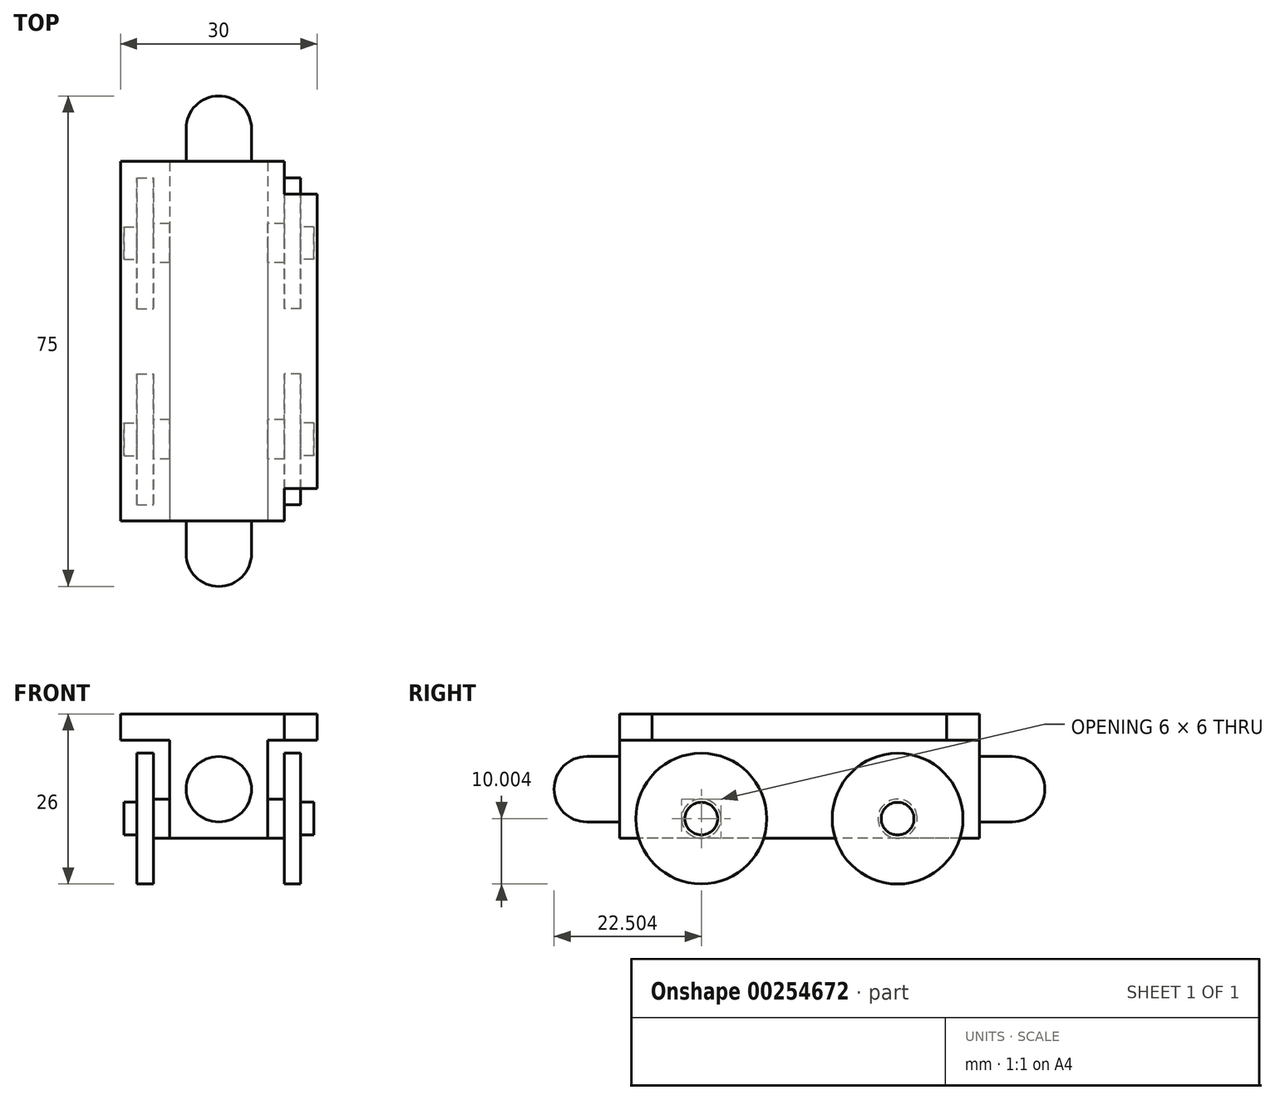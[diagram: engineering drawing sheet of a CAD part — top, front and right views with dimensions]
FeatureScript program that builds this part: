
annotation { "Feature Type Name" : "Feature", "Feature Type Description" : "" }
export const myFeature = defineFeature(function(context is Context, id is Id, definition is map)
    precondition{}
    {
        {
            var Q0;
            Q0=qCreatedBy(makeId("Top.planeOp"),FACE);
            var sketch = newSketch(context, id + "F0", { "sketchPlane" : qUnion([Q0])});
            skLineSegment(sketch, "E0.bottom", {"start": v(7.5, 27.5) * mm, "end": v(-7.5, 27.5) * mm});
            skLineSegment(sketch, "E0.top", {"start": v(7.5, -27.5) * mm, "end": v(-7.5, -27.5) * mm});
            skLineSegment(sketch, "E0.left", {"start": v(7.5, 27.5) * mm, "end": v(7.5, -27.5) * mm});
            skLineSegment(sketch, "E0.right", {"start": v(-7.5, 27.5) * mm, "end": v(-7.5, -27.5) * mm});
            skPoint(sketch, "E0.middle", {"position": v(0, 0) * mm});
            skSolve(sketch);
        }
        {
            var Q0;
            Q0 = qSketchRegion(id + "F0", true);
            extrude(context, id + "F1", {"entities" : qUnion([Q0]), "oppositeDirection" : true, "depth" : 15 * mm});
        }
        {
            var Q0;
            Q0=qCreatedBy(makeId("Top.planeOp"),FACE);
            var sketch = newSketch(context, id + "F2", { "sketchPlane" : qUnion([Q0])});
            skLineSegment(sketch, "E1.bottom", {"start": v(15, 27.5) * mm, "end": v(-15, 27.5) * mm});
            skLineSegment(sketch, "E1.top", {"start": v(15, -27.5) * mm, "end": v(-15, -27.5) * mm});
            skLineSegment(sketch, "E1.left", {"start": v(15, 27.5) * mm, "end": v(15, -27.5) * mm});
            skLineSegment(sketch, "E1.right", {"start": v(-15, 27.5) * mm, "end": v(-15, -27.5) * mm});
            skPoint(sketch, "E1.middle", {"position": v(0, 0) * mm});
            skSolve(sketch);
        }
        {
            var Q0;
            Q0 = qSketchRegion(id + "F2", true);
            extrude(context, id + "F3", {"entities" : qUnion([Q0]), "operationType" : NewBodyOperationType.ADD, "depth" : 4 * mm});
        }
        {
            var Q0;
            Q0=qCreatedBy(makeId("Top.planeOp"),FACE);
            var sketch = newSketch(context, id + "F4", { "sketchPlane" : qUnion([Q0])});
            skPoint(sketch, "E2.0", {"position": v(15, -27.5) * mm});
            skPoint(sketch, "E3.0", {"position": v(15, 27.5) * mm});
            skLineSegment(sketch, "E4", {"start": v(15, -27.5) * mm, "end": v(10, -27.5) * mm});
            skLineSegment(sketch, "E5", {"start": v(15, -27.5) * mm, "end": v(15, -22.5) * mm});
            skLineSegment(sketch, "E6.bottom", {"start": v(15, -22.5) * mm, "end": v(10, -22.5) * mm});
            skLineSegment(sketch, "E6.left", {"start": v(15, -22.5) * mm, "end": v(15, -27.5) * mm});
            skLineSegment(sketch, "E6.right", {"start": v(10, -22.5) * mm, "end": v(10, -27.5) * mm});
            skSolve(sketch);
        }
        {
            var Q0;
            Q0 = qSketchRegion(id + "F4", true);
            extrude(context, id + "F5", {"entities" : qUnion([Q0]), "operationType" : NewBodyOperationType.REMOVE, "depth" : 25 * mm});
        }
        {
            var Q0;
            Q0=qCreatedBy(makeId("Top.planeOp"),FACE);
            var sketch = newSketch(context, id + "F6", { "sketchPlane" : qUnion([Q0])});
            skPoint(sketch, "E7.0", {"position": v(15, 27.5) * mm});
            skLineSegment(sketch, "E8", {"start": v(15, 27.5) * mm, "end": v(10, 27.5) * mm});
            skLineSegment(sketch, "E9", {"start": v(15, 27.5) * mm, "end": v(15, 22.5) * mm});
            skLineSegment(sketch, "E10.bottom", {"start": v(10, 27.5) * mm, "end": v(15, 27.5) * mm});
            skLineSegment(sketch, "E10.top", {"start": v(10, 22.5) * mm, "end": v(15, 22.5) * mm});
            skLineSegment(sketch, "E10.left", {"start": v(10, 27.5) * mm, "end": v(10, 22.5) * mm});
            skSolve(sketch);
        }
        {
            var Q0;
            Q0 = qSketchRegion(id + "F6", true);
            extrude(context, id + "F7", {"entities" : qUnion([Q0]), "operationType" : NewBodyOperationType.REMOVE, "depth" : 25 * mm});
        }
        {
            var Q0;
            Q0=makeQuery(id+"F3.boolean.opBoolean","MERGE",FACE,{"derivedFrom":[makeQuery(id+"F1.opExtrude","SWEPT_FACE",FACE,{"disambiguationData":[OSD([sQuery(id+"F0.wireOp",EDGE,"E0.top")])]}),makeQuery(id+"F3.opExtrude","SWEPT_FACE",FACE,{"disambiguationData":[OSD([sQuery(id+"F2.wireOp",EDGE,"E1.top")])]})]});
            var sketch = newSketch(context, id + "F8", { "sketchPlane" : qUnion([Q0])});
            skLineSegment(sketch, "E11", {"start": v(0, -15) * mm, "end": v(0, -7.5) * mm, "construction": true});
            skPoint(sketch, "E11.endSnap0", {"position": v(0, -15) * mm});
            skCircle(sketch, "E12", {"center": v(0, -7.5) * mm, "radius": 5 * mm});
            skSolve(sketch);
        }
        {
            var Q0;
            Q0 = qSketchRegion(id + "F8", true);
            extrude(context, id + "F9", {"entities" : qUnion([Q0]), "operationType" : NewBodyOperationType.ADD, "depth" : 5 * mm});
        }
        {
            var Q0;
            Q0=makeQuery(id+"F3.boolean.opBoolean","MERGE",FACE,{"derivedFrom":[makeQuery(id+"F1.opExtrude","SWEPT_FACE",FACE,{"disambiguationData":[OSD([sQuery(id+"F0.wireOp",EDGE,"E0.bottom")])]}),makeQuery(id+"F3.opExtrude","SWEPT_FACE",FACE,{"disambiguationData":[OSD([sQuery(id+"F2.wireOp",EDGE,"E1.bottom")])]})]});
            var sketch = newSketch(context, id + "F10", { "sketchPlane" : qUnion([Q0])});
            skLineSegment(sketch, "E13", {"start": v(0, -15) * mm, "end": v(0, -7.5) * mm, "construction": true});
            skPoint(sketch, "E13.endSnap0", {"position": v(0, -15) * mm});
            skCircle(sketch, "E14", {"center": v(0, -7.5) * mm, "radius": 5 * mm});
            skSolve(sketch);
        }
        {
            var Q0;
            Q0 = qSketchRegion(id + "F10", true);
            extrude(context, id + "F11", {"entities" : qUnion([Q0]), "operationType" : NewBodyOperationType.ADD, "depth" : 5 * mm});
        }
        {
            var Q0;
            Q0=qCreatedBy(makeId("Right.planeOp"),FACE);
            var sketch = newSketch(context, id + "F12", { "sketchPlane" : qUnion([Q0])});
            skLineSegment(sketch, "E15", {"start": v(-27.5, -15) * mm, "end": v(-15, -15) * mm, "construction": true});
            skLineSegment(sketch, "E16", {"start": v(-15, -15) * mm, "end": v(-15, -12) * mm, "construction": true});
            skCircle(sketch, "E17", {"center": v(-15, -12) * mm, "radius": 3 * mm});
            skSolve(sketch);
        }
        {
            var Q0;
            Q0 = qSketchRegion(id + "F12", true);
            extrude(context, id + "F13", {"entities" : qUnion([Q0]), "operationType" : NewBodyOperationType.ADD, "endBound" : BoundingType.SYMMETRIC, "depth" : 20 * mm});
        }
        {
            var Q0;
            Q0=qCreatedBy(makeId("Right.planeOp"),FACE);
            var sketch = newSketch(context, id + "F14", { "sketchPlane" : qUnion([Q0])});
            skPoint(sketch, "E18.0", {"position": v(27.5, -15) * mm});
            skLineSegment(sketch, "E19", {"start": v(27.5, -15) * mm, "end": v(15, -15) * mm, "construction": true});
            skLineSegment(sketch, "E20", {"start": v(15, -15) * mm, "end": v(15, -12) * mm, "construction": true});
            skCircle(sketch, "E21", {"center": v(15, -12) * mm, "radius": 3 * mm});
            skSolve(sketch);
        }
        {
            var Q0;
            Q0 = qSketchRegion(id + "F14", true);
            extrude(context, id + "F15", {"entities" : qUnion([Q0]), "operationType" : NewBodyOperationType.ADD, "endBound" : BoundingType.SYMMETRIC, "depth" : 20 * mm});
        }
        {
            var Q0;
            Q0=makeQuery(id+"F13.opExtrude","CAP_FACE",FACE,{"disambiguationData":[OSD([sQuery(id+"F12.wireOp",EDGE,"E17")])],"isStart":false});
            var sketch = newSketch(context, id + "F16", { "sketchPlane" : qUnion([Q0])});
            skPoint(sketch, "E22", {"position": v(-15, -12) * mm});
            skCircle(sketch, "E23", {"center": v(-15, -12) * mm, "radius": 10 * mm});
            skSolve(sketch);
        }
        {
            var Q0;
            Q0 = qSketchRegion(id + "F16", true);
            extrude(context, id + "F17", {"entities" : qUnion([Q0]), "operationType" : NewBodyOperationType.ADD, "depth" : 2.5 * mm});
        }
        {
            var Q0;
            Q0=makeQuery(id+"F15.opExtrude","CAP_FACE",FACE,{"disambiguationData":[OSD([sQuery(id+"F14.wireOp",EDGE,"E21")])],"isStart":false});
            var sketch = newSketch(context, id + "F18", { "sketchPlane" : qUnion([Q0])});
            skPoint(sketch, "E24", {"position": v(15, -12) * mm});
            skCircle(sketch, "E25", {"center": v(15, -12) * mm, "radius": 10 * mm});
            skSolve(sketch);
        }
        {
            var Q0;
            Q0 = qSketchRegion(id + "F18", true);
            extrude(context, id + "F19", {"entities" : qUnion([Q0]), "operationType" : NewBodyOperationType.ADD, "depth" : 2.5 * mm});
        }
        {
            var Q0;
            Q0=makeQuery(id+"F15.opExtrude","CAP_FACE",FACE,{"disambiguationData":[OSD([sQuery(id+"F14.wireOp",EDGE,"E21")])],"isStart":true});
            var sketch = newSketch(context, id + "F20", { "sketchPlane" : qUnion([Q0])});
            skPoint(sketch, "E26", {"position": v(-15, -12) * mm});
            skCircle(sketch, "E27", {"center": v(-15, -12) * mm, "radius": 10 * mm});
            skSolve(sketch);
        }
        {
            var Q0;
            Q0 = qSketchRegion(id + "F20", true);
            extrude(context, id + "F21", {"entities" : qUnion([Q0]), "operationType" : NewBodyOperationType.ADD, "depth" : 2.5 * mm});
        }
        {
            var Q0;
            Q0=makeQuery(id+"F13.opExtrude","CAP_FACE",FACE,{"disambiguationData":[OSD([sQuery(id+"F12.wireOp",EDGE,"E17")])],"isStart":true});
            var sketch = newSketch(context, id + "F22", { "sketchPlane" : qUnion([Q0])});
            skPoint(sketch, "E28", {"position": v(15, -12) * mm});
            skCircle(sketch, "E29", {"center": v(15, -12) * mm, "radius": 10 * mm});
            skSolve(sketch);
        }
        {
            var Q0;
            Q0 = qSketchRegion(id + "F22", true);
            extrude(context, id + "F23", {"entities" : qUnion([Q0]), "operationType" : NewBodyOperationType.ADD, "depth" : 2.5 * mm});
        }
        {
            var Q0;
            Q0=makeQuery(id+"F17.opExtrude","CAP_FACE",FACE,{"disambiguationData":[OSD([sQuery(id+"F16.wireOp",EDGE,"E23")])],"isStart":false});
            var sketch = newSketch(context, id + "F24", { "sketchPlane" : qUnion([Q0])});
            skPoint(sketch, "E30", {"position": v(-15, -12) * mm});
            skCircle(sketch, "E31", {"center": v(-15, -12) * mm, "radius": 2.5 * mm});
            skSolve(sketch);
        }
        {
            var Q0;
            Q0 = qSketchRegion(id + "F24", true);
            extrude(context, id + "F25", {"entities" : qUnion([Q0]), "operationType" : NewBodyOperationType.ADD, "depth" : 2 * mm});
        }
        {
            var Q0;
            Q0=makeQuery(id+"F19.opExtrude","CAP_FACE",FACE,{"disambiguationData":[OSD([sQuery(id+"F18.wireOp",EDGE,"E25")])],"isStart":false});
            var sketch = newSketch(context, id + "F26", { "sketchPlane" : qUnion([Q0])});
            skPoint(sketch, "E32", {"position": v(15, -12) * mm});
            skCircle(sketch, "E33", {"center": v(15, -12) * mm, "radius": 2.5 * mm});
            skSolve(sketch);
        }
        {
            var Q0;
            Q0 = qSketchRegion(id + "F26", true);
            extrude(context, id + "F27", {"entities" : qUnion([Q0]), "operationType" : NewBodyOperationType.ADD, "depth" : 2 * mm});
        }
        {
            var Q0;
            Q0=makeQuery(id+"F23.opExtrude","CAP_FACE",FACE,{"disambiguationData":[OSD([sQuery(id+"F22.wireOp",EDGE,"E29")])],"isStart":false});
            var sketch = newSketch(context, id + "F28", { "sketchPlane" : qUnion([Q0])});
            skPoint(sketch, "E34", {"position": v(15, -12) * mm});
            skCircle(sketch, "E35", {"center": v(15, -12) * mm, "radius": 2.5 * mm});
            skSolve(sketch);
        }
        {
            var Q0;
            Q0 = qSketchRegion(id + "F28", true);
            extrude(context, id + "F29", {"entities" : qUnion([Q0]), "operationType" : NewBodyOperationType.ADD, "depth" : 2 * mm});
        }
        {
            var Q0;
            Q0=makeQuery(id+"F21.opExtrude","CAP_FACE",FACE,{"disambiguationData":[OSD([sQuery(id+"F20.wireOp",EDGE,"E27")])],"isStart":false});
            var sketch = newSketch(context, id + "F30", { "sketchPlane" : qUnion([Q0])});
            skPoint(sketch, "E36", {"position": v(-15, -12) * mm});
            skCircle(sketch, "E37", {"center": v(-15, -12) * mm, "radius": 2.5 * mm});
            skSolve(sketch);
        }
        {
            var Q0;
            Q0 = qSketchRegion(id + "F30", true);
            extrude(context, id + "F31", {"entities" : qUnion([Q0]), "operationType" : NewBodyOperationType.ADD, "depth" : 2 * mm});
        }
        {
            var Q0;
            Q0=makeQuery(id+"F11.opExtrude","CAP_FACE",FACE,{"disambiguationData":[OSD([sQuery(id+"F10.wireOp",EDGE,"E14")])],"isStart":false});
            var sketch = newSketch(context, id + "F32", { "sketchPlane" : qUnion([Q0])});
            skPoint(sketch, "E38", {"position": v(0, -7.5) * mm});
            skArc(sketch, "E39", {"start": v(0, -12.5) * mm, "mid": v(5, -7.5) * mm, "end": v(0, -2.5) * mm});
            skLineSegment(sketch, "E40", {"start": v(0, -2.5) * mm, "end": v(0, -12.5) * mm});
            skSolve(sketch);
        }
        {
            var Q0;
            Q0 = qSketchRegion(id + "F32", true);
            var Q1;
            Q1=sQuery(id+"F32.wireOp",EDGE,"E40");
            revolve(context, id + "F33", {"operationType" : NewBodyOperationType.ADD, "entities" : qUnion([Q0]), "axis" : qUnion([Q1]), "revolveType" : RevolveType.FULL});
        }
        {
            var Q0;
            Q0=makeQuery(id+"F9.opExtrude","CAP_FACE",FACE,{"disambiguationData":[OSD([sQuery(id+"F8.wireOp",EDGE,"E12")])],"isStart":false});
            var sketch = newSketch(context, id + "F34", { "sketchPlane" : qUnion([Q0])});
            skPoint(sketch, "E41", {"position": v(0, -7.5) * mm});
            skArc(sketch, "E42", {"start": v(0, -12.5) * mm, "mid": v(5, -7.5) * mm, "end": v(0, -2.5) * mm});
            skLineSegment(sketch, "E43", {"start": v(0, -2.5) * mm, "end": v(0, -12.5) * mm});
            skSolve(sketch);
        }
        {
            var Q0;
            Q0 = qSketchRegion(id + "F34", true);
            var Q1;
            Q1=sQuery(id+"F34.wireOp",EDGE,"E43");
            revolve(context, id + "F35", {"operationType" : NewBodyOperationType.ADD, "entities" : qUnion([Q0]), "axis" : qUnion([Q1]), "revolveType" : RevolveType.FULL});
        }
    });
